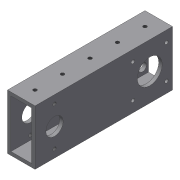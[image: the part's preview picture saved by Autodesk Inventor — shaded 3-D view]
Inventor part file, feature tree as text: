
AUTODESK INVENTOR PART (.ipt)
format: ipt  version: 2018 (Build 220112000, 112)  size: 161,280 bytes
history: native  units: mm
features: sketch x6, hole x4, extrude x3, other x3, shell x1, pattern_linear x1, reference x1
ambient origin geometry x8: Origin, YZ Plane, XZ Plane, XY Plane, X Axis, Y Axis, Z Axis, Center Point
bodies: Solid1 (feature_tree)
feature tree (19):
  extrude  "Extrusion1"  Depth=25.4mm
  shell  "Shell1"  Thickness=127.0mm
  sketch  "Sketch2"  dims[d4=3.175mm d5=31.0mm]
  hole  "Hole1"  [1 undecoded]
  hole  "Hole2"  [1 undecoded]
  extrude  "Extrusion2"  Depth=8.0mm
  extrude  "Extrusion3"  Depth=50.8mm
  hole  "Hole4"  [1 undecoded]
  hole  "Hole5"  [1 undecoded]
  pattern_linear  "Rectangular Pattern1"  Spacing1=36.0mm  [1 undecoded]
  sketch  "Sketch1"  dims[d0=50.8mm d1=25.4mm d2=127.0mm d3=0.0mm]
  sketch  "Sketch3"  dims[d6=31.0mm d7=21.0mm]
  sketch  "Sketch4"  dims[d8=3.2mm d9=6.0mm d10=7.5mm d11=5.0mm d12=90.0deg d13=8.0mm d14=20.594885mm]
  sketch  "Sketch6"  dims[d15=10.0mm d16=6.0mm d17=6.5mm d18=3.0mm d19=90.0deg d20=8.0mm d21=20.594885mm d22=23.0mm]
  sketch  "Sketch7"  dims[d23=50.8mm d24=0.0mm d25=16.0mm d26=18.0mm d27=50.8mm d28=0.0mm d40=3.242mm d41=100.0mm d42=6.5mm d43=3.0mm d44=90.0deg d45=11.8mm d46=20.594885mm d47=36.0mm d48=3.242mm d49=100.0mm d50=6.5mm d51=3.0mm d52=90.0deg d53=11.8mm d54=20.594885mm d55=50.8mm d57=20.0mm d59=50.8mm d61=38.1mm]
  reference  "Reference1"
  parser-record x1  (decoder bookkeeping rows leaked as tree rows — omitted from the tree; the rows remain in map.json)
  other  "AMR_Transm2.iam"
  other  "7804K147_STAINLESS STEEL BALL BEARING:2"
note: 5 required parameter values undecoded (feature->parameter linkage not recoverable at this tier; creation-order binding heuristic only, values carry confidence <= 0.55)
note: 1 file-system path scrubbed to <path> (originals preserved in map.json)
